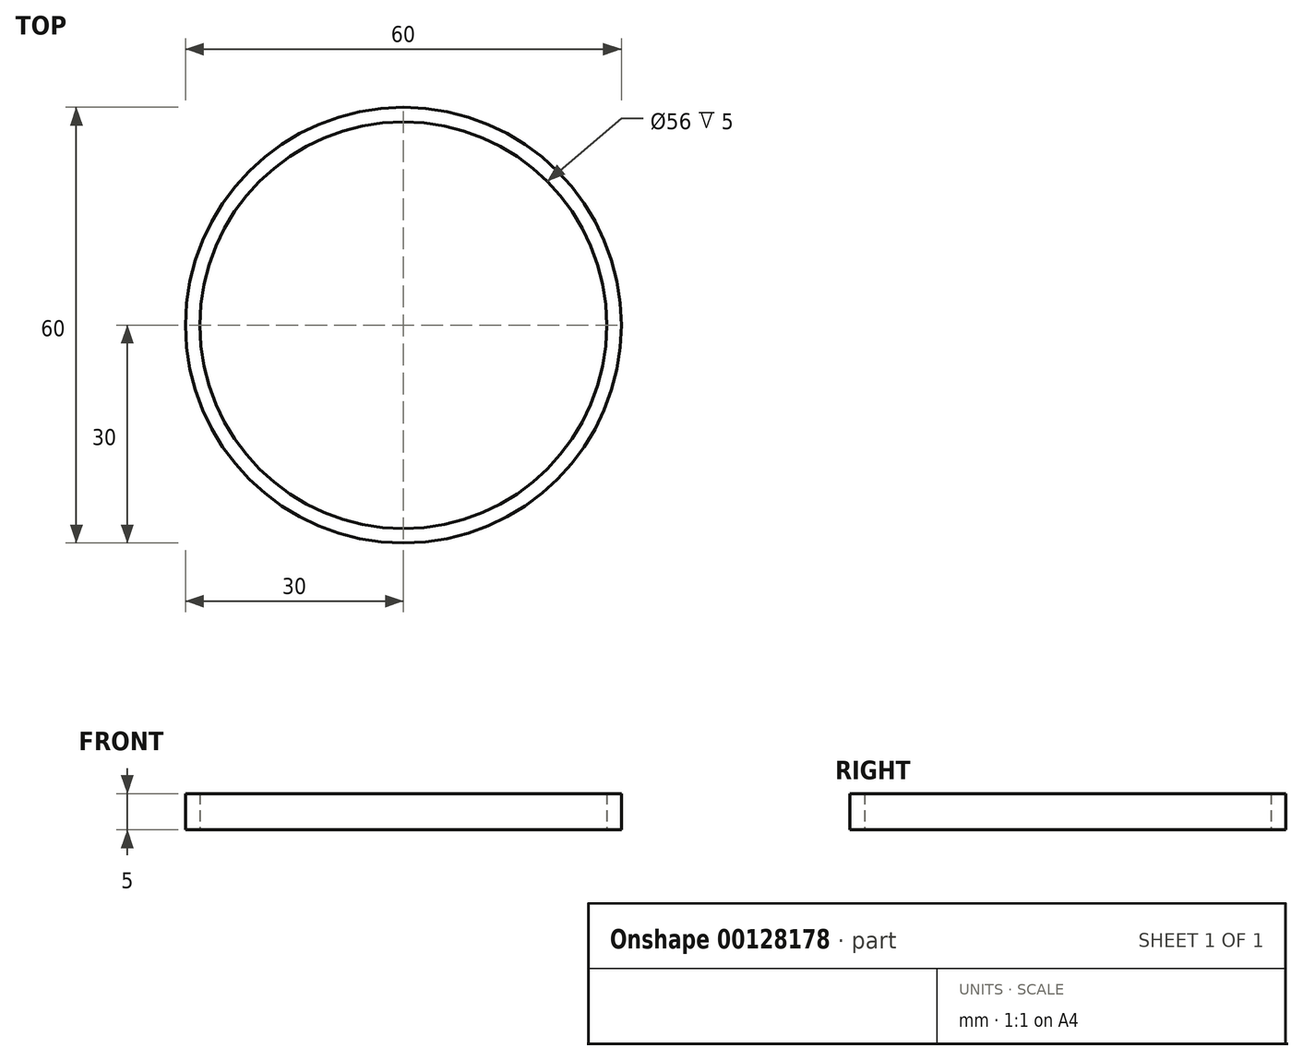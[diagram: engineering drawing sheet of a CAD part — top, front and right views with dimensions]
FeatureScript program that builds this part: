
annotation { "Feature Type Name" : "Feature", "Feature Type Description" : "" }
export const myFeature = defineFeature(function(context is Context, id is Id, definition is map)
    precondition{}
    {
        {
            var Q0;
            Q0=qCreatedBy(makeId("Front.planeOp"),FACE);
            var sketch = newSketch(context, id + "F0", { "sketchPlane" : qUnion([Q0])});
            skLineSegment(sketch, "E0.bottom", {"start": v(28, 94.29) * mm, "end": v(30, 94.29) * mm});
            skLineSegment(sketch, "E0.top", {"start": v(28, 99.29) * mm, "end": v(30, 99.29) * mm});
            skLineSegment(sketch, "E0.left", {"start": v(0, 94.29) * mm, "end": v(0, 99.29) * mm});
            skLineSegment(sketch, "E0.right", {"start": v(30, 94.29) * mm, "end": v(30, 99.29) * mm});
            skLineSegment(sketch, "E1", {"start": v(28, 99.29) * mm, "end": v(28, 94.29) * mm});
            skSolve(sketch);
        }
        {
            var Q0;
            Q0=makeQuery(id+"F0.imprint","IMPRINT",FACE,{"disambiguationData":[TD([[makeQuery(id+"F0.imprint","IMPRINT",EDGE,{"derivedFrom":sQuery(id+"F0.wireOp",EDGE,"E0.bottom")}),1.0]])]});
            var Q1;
            Q1=sQuery(id+"F0.wireOp",EDGE,"E0.left");
            revolve(context, id + "F1", {"entities" : qUnion([Q0]), "axis" : qUnion([Q1]), "revolveType" : RevolveType.FULL});
        }
    });
